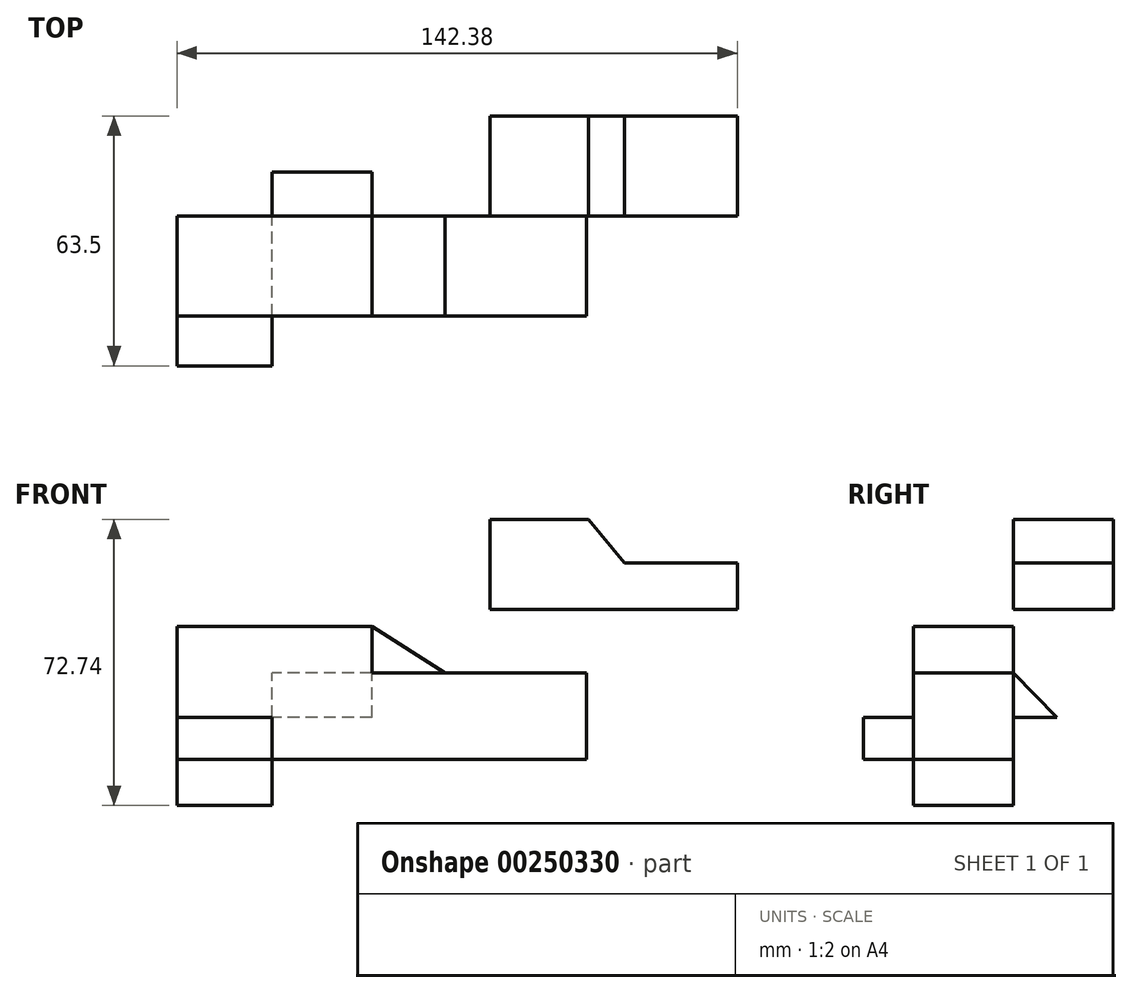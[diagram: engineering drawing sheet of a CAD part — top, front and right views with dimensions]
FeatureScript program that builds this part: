
annotation { "Feature Type Name" : "Feature", "Feature Type Description" : "" }
export const myFeature = defineFeature(function(context is Context, id is Id, definition is map)
    precondition{}
    {
        {
            var Q0;
            Q0=qCreatedBy(makeId("Front.planeOp"),FACE);
            var sketch = newSketch(context, id + "F0", { "sketchPlane" : qUnion([Q0])});
            skLineSegment(sketch, "E0", {"start": v(-75.52, 11.3) * mm, "end": v(-43.02, 11.3) * mm});
            skLineSegment(sketch, "E1", {"start": v(-43.02, 11.3) * mm, "end": v(-43.02, 0) * mm});
            skLineSegment(sketch, "E2", {"start": v(-43.02, 0) * mm, "end": v(-75.52, 0) * mm});
            skLineSegment(sketch, "E3", {"start": v(-75.52, 0) * mm, "end": v(-75.52, 11.3) * mm});
            skLineSegment(sketch, "E4", {"start": v(-43.02, 11.3) * mm, "end": v(-29.4, 11.3) * mm});
            skLineSegment(sketch, "E5", {"start": v(-29.4, 11.3) * mm, "end": v(28.48, 11.3) * mm});
            skLineSegment(sketch, "E6", {"start": v(28.48, 11.3) * mm, "end": v(28.48, 0) * mm});
            skLineSegment(sketch, "E7", {"start": v(-75.52, 0) * mm, "end": v(-75.52, -10.68) * mm});
            skLineSegment(sketch, "E8", {"start": v(-75.52, -10.68) * mm, "end": v(-28.17, -10.68) * mm});
            skLineSegment(sketch, "E9", {"start": v(-28.17, -10.68) * mm, "end": v(-28.17, 0) * mm});
            skLineSegment(sketch, "E10", {"start": v(-43.02, 0) * mm, "end": v(-43.02, -10.68) * mm});
            skLineSegment(sketch, "E11", {"start": v(28.48, 0) * mm, "end": v(28.48, -10.68) * mm});
            skLineSegment(sketch, "E12", {"start": v(28.48, -10.68) * mm, "end": v(-28.17, -10.68) * mm});
            skPoint(sketch, "E13.start.orphan", {"position": v(-29.4, 0) * mm});
            skLineSegment(sketch, "E14", {"start": v(-28.17, 0) * mm, "end": v(-28.17, 11.3) * mm});
            skLineSegment(sketch, "E15", {"start": v(-75.52, -10.68) * mm, "end": v(-75.52, -22.44) * mm});
            skLineSegment(sketch, "E16", {"start": v(-75.52, -22.44) * mm, "end": v(-51.38, -22.44) * mm});
            skLineSegment(sketch, "E17", {"start": v(-51.38, -22.44) * mm, "end": v(-51.38, -10.68) * mm});
            skLineSegment(sketch, "E18", {"start": v(-75.52, 11.3) * mm, "end": v(-75.52, 23.06) * mm});
            skLineSegment(sketch, "E19", {"start": v(-75.52, 23.06) * mm, "end": v(-51.38, 23.06) * mm});
            skLineSegment(sketch, "E20", {"start": v(-51.38, 23.06) * mm, "end": v(-51.38, 11.3) * mm});
            skSolve(sketch);
        }
        {
            var Q0;
            Q0=makeQuery(id+"F0.imprint","IMPRINT",FACE,{"disambiguationData":[TD([[makeQuery(id+"F0.imprint","IMPRINT",EDGE,{"derivedFrom":sQuery(id+"F0.wireOp",EDGE,"E1")}),1.0]])]});
            var Q1;
            {var subQ1=sQuery(id+"F0.wireOp",EDGE,"E6");Q1=makeQuery(id+"F0.imprint","IMPRINT",FACE,{"disambiguationData":[TD([[makeQuery(id+"F0.imprint","IMPRINT",EDGE,{"derivedFrom":subQ1}),-1.0]])]});}
            var Q2;
            {var subQ0=sQuery(id+"F0.wireOp",EDGE,"E18");Q2=makeQuery(id+"F0.imprint","IMPRINT",FACE,{"disambiguationData":[TD([[makeQuery(id+"F0.imprint","IMPRINT",EDGE,{"derivedFrom":subQ0}),-1.0]])]});}
            var Q3;
            {var subQ0=sQuery(id+"F0.wireOp",EDGE,"E1");Q3=makeQuery(id+"F0.imprint","IMPRINT",FACE,{"disambiguationData":[TD([[makeQuery(id+"F0.imprint","IMPRINT",EDGE,{"derivedFrom":subQ0}),-1.0]])]});}
            var Q4;
            {var subQ0=sQuery(id+"F0.wireOp",EDGE,"E15");Q4=makeQuery(id+"F0.imprint","IMPRINT",FACE,{"disambiguationData":[TD([[makeQuery(id+"F0.imprint","IMPRINT",EDGE,{"derivedFrom":subQ0}),1.0]])]});}
            var Q5;
            Q5=makeQuery(id+"F0.imprint","IMPRINT",FACE,{"disambiguationData":[TD([[makeQuery(id+"F0.imprint","IMPRINT",EDGE,{"derivedFrom":sQuery(id+"F0.wireOp",EDGE,"E2")}),1.0]])]});
            extrude(context, id + "F1", {"entities" : qUnion([Q0, Q1, Q2, Q3, Q4, Q5]), "depth" : 25.4 * mm});
        }
        {
            var Q0;
            Q0=makeQuery(id+"F1.opExtrude","SWEPT_FACE",FACE,{"disambiguationData":[OSD([sQuery(id+"F0.wireOp",EDGE,"E20")])]});
            var sketch = newSketch(context, id + "F2", { "sketchPlane" : qUnion([Q0])});
            skLineSegment(sketch, "E21", {"start": v(-25.4, 23.06) * mm, "end": v(-25.4, 11.3) * mm});
            skLineSegment(sketch, "E22", {"start": v(-25.4, 11.3) * mm, "end": v(-14.19, 0) * mm});
            skLineSegment(sketch, "E23", {"start": v(-14.19, 0) * mm, "end": v(11.08, 0) * mm});
            skLineSegment(sketch, "E24", {"start": v(11.08, 0) * mm, "end": v(0, 11.3) * mm});
            skLineSegment(sketch, "E25", {"start": v(0, 11.3) * mm, "end": v(0, 23.06) * mm});
            skLineSegment(sketch, "E26", {"start": v(0, 23.06) * mm, "end": v(-23.55, 23.06) * mm});
            skLineSegment(sketch, "E27", {"start": v(-23.55, 23.06) * mm, "end": v(-25.4, 23.06) * mm});
            skSolve(sketch);
        }
        {
            var Q0;
            Q0 = qSketchRegion(id + "F2", true);
            extrude(context, id + "F3", {"entities" : qUnion([Q0]), "operationType" : NewBodyOperationType.ADD, "depth" : 25.4 * mm});
        }
        {
            var Q0;
            Q0=makeQuery(id+"F3.boolean.opBoolean","MERGE",FACE,{"derivedFrom":[makeQuery(id+"F1.opExtrude","CAP_FACE",FACE,{"disambiguationData":[OSD([sQuery(id+"F0.wireOp",EDGE,"E0"),sQuery(id+"F0.wireOp",EDGE,"E3"),sQuery(id+"F0.wireOp",EDGE,"E4"),sQuery(id+"F0.wireOp",EDGE,"E5"),sQuery(id+"F0.wireOp",EDGE,"E6"),sQuery(id+"F0.wireOp",EDGE,"E7"),sQuery(id+"F0.wireOp",EDGE,"E8"),sQuery(id+"F0.wireOp",EDGE,"E11"),sQuery(id+"F0.wireOp",EDGE,"E12"),sQuery(id+"F0.wireOp",EDGE,"E15"),sQuery(id+"F0.wireOp",EDGE,"E16"),sQuery(id+"F0.wireOp",EDGE,"E17"),sQuery(id+"F0.wireOp",EDGE,"E18"),sQuery(id+"F0.wireOp",EDGE,"E19"),sQuery(id+"F0.wireOp",EDGE,"E20")])],"isStart":false}),makeQuery(id+"F3.opExtrude","SWEPT_FACE",FACE,{"disambiguationData":[OSD([sQuery(id+"F2.wireOp",EDGE,"E21")])]})]});
            var sketch = newSketch(context, id + "F4", { "sketchPlane" : qUnion([Q0])});
            skLineSegment(sketch, "E28", {"start": v(-51.38, -10.68) * mm, "end": v(-75.52, -10.68) * mm});
            skLineSegment(sketch, "E29", {"start": v(-51.38, -10.68) * mm, "end": v(-51.38, 0) * mm});
            skLineSegment(sketch, "E30", {"start": v(-51.38, 0) * mm, "end": v(-75.52, 0) * mm});
            skSolve(sketch);
        }
        {
            var Q0;
            {var subQ0=sQuery(id+"F4.wireOp",EDGE,"E28");Q0=makeQuery(id+"F4.imprint","IMPRINT",FACE,{"disambiguationData":[TD([[makeQuery(id+"F4.imprint","IMPRINT",EDGE,{"derivedFrom":subQ0}),-1.0]])]});}
            extrude(context, id + "F5", {"entities" : qUnion([Q0]), "operationType" : NewBodyOperationType.ADD, "depth" : 12.7 * mm});
        }
        {
            var Q0;
            Q0=qCreatedBy(makeId("Front.planeOp"),FACE);
            var sketch = newSketch(context, id + "F6", { "sketchPlane" : qUnion([Q0])});
            skLineSegment(sketch, "E31", {"start": v(4.02, 27.4) * mm, "end": v(66.86, 27.4) * mm});
            skLineSegment(sketch, "E32", {"start": v(66.86, 27.4) * mm, "end": v(66.86, 39.15) * mm});
            skLineSegment(sketch, "E33", {"start": v(66.86, 39.15) * mm, "end": v(38.17, 39.15) * mm});
            skLineSegment(sketch, "E34", {"start": v(29.1, 50.3) * mm, "end": v(4.02, 50.3) * mm});
            skLineSegment(sketch, "E35", {"start": v(4.02, 50.3) * mm, "end": v(4.02, 27.4) * mm});
            skLineSegment(sketch, "E36", {"start": v(29.1, 50.3) * mm, "end": v(38.17, 39.15) * mm});
            skLineSegment(sketch, "E37", {"start": v(4.02, 34.55) * mm, "end": v(15.04, 34.55) * mm});
            skLineSegment(sketch, "E38", {"start": v(15.04, 34.55) * mm, "end": v(15.04, 25.13) * mm});
            skSolve(sketch);
        }
        {
            var Q0;
            {var subQ1=sQuery(id+"F6.wireOp",EDGE,"E32");Q0=makeQuery(id+"F6.imprint","IMPRINT",FACE,{"disambiguationData":[TD([[makeQuery(id+"F6.imprint","IMPRINT",EDGE,{"derivedFrom":subQ1}),1.0]])]});}
            var Q1;
            {var subQ5=sQuery(id+"F6.wireOp",EDGE,"E37");Q1=makeQuery(id+"F6.imprint","IMPRINT",FACE,{"disambiguationData":[TD([[makeQuery(id+"F6.imprint","IMPRINT",EDGE,{"derivedFrom":subQ5}),-1.0]])]});}
            extrude(context, id + "F7", {"entities" : qUnion([Q0, Q1]), "oppositeDirection" : true, "depth" : 25.4 * mm});
        }
        {
            var Q0;
            {var subQ2=sQuery(id+"F2.wireOp",EDGE,"E21");var subQ3=makeQuery(id+"F3.opExtrude","SWEPT_FACE",FACE,{"disambiguationData":[OSD([subQ2])]});var subQ4=sQuery(id+"F0.wireOp",EDGE,"E17");var subQ5=sQuery(id+"F0.wireOp",EDGE,"E12");var subQ6=sQuery(id+"F0.wireOp",EDGE,"E8");var subQ7=sQuery(id+"F0.wireOp",EDGE,"E19");var subQ8=sQuery(id+"F0.wireOp",EDGE,"E18");var subQ9=sQuery(id+"F0.wireOp",EDGE,"E15");var subQ10=sQuery(id+"F0.wireOp",EDGE,"E11");var subQ11=sQuery(id+"F0.wireOp",EDGE,"E7");var subQ12=sQuery(id+"F0.wireOp",EDGE,"E6");var subQ13=sQuery(id+"F0.wireOp",EDGE,"E5");var subQ14=sQuery(id+"F0.wireOp",EDGE,"E4");var subQ15=sQuery(id+"F0.wireOp",EDGE,"E3");var subQ16=sQuery(id+"F0.wireOp",EDGE,"E0");var subQ17=makeQuery(id+"F1.opExtrude","CAP_FACE",FACE,{"disambiguationData":[OSD([subQ16,subQ15,subQ14,subQ13,subQ12,subQ11,subQ6,subQ10,subQ5,subQ9,sQuery(id+"F0.wireOp",EDGE,"E16"),subQ4,subQ8,subQ7,sQuery(id+"F0.wireOp",EDGE,"E20")])],"isStart":false});Q0=makeQuery(id+"F5.boolean.opBoolean","SPLIT",FACE,{"disambiguationData":[TD([makeQuery(id+"F1.opExtrude","SWEPT_FACE",FACE,{"disambiguationData":[OSD([subQ7])]})])],"derivedFrom":makeQuery(id+"F3.boolean.opBoolean","MERGE",FACE,{"derivedFrom":[subQ17,subQ3]})});}
            var sketch = newSketch(context, id + "F8", { "sketchPlane" : qUnion([Q0])});
            skLineSegment(sketch, "E39", {"start": v(-25.98, 23.06) * mm, "end": v(-7.43, 11.3) * mm});
            skSolve(sketch);
        }
        {
            var Q0;
            {var subQ0=sQuery(id+"F8.wireOp",EDGE,"E39");Q0=makeQuery(id+"F8.imprint","IMPRINT",FACE,{"disambiguationData":[TD([[makeQuery(id+"F8.imprint","IMPRINT",EDGE,{"derivedFrom":subQ0}),-1.0]])]});}
            extrude(context, id + "F9", {"entities" : qUnion([Q0]), "oppositeDirection" : true, "depth" : 25.4 * mm});
        }
    });
